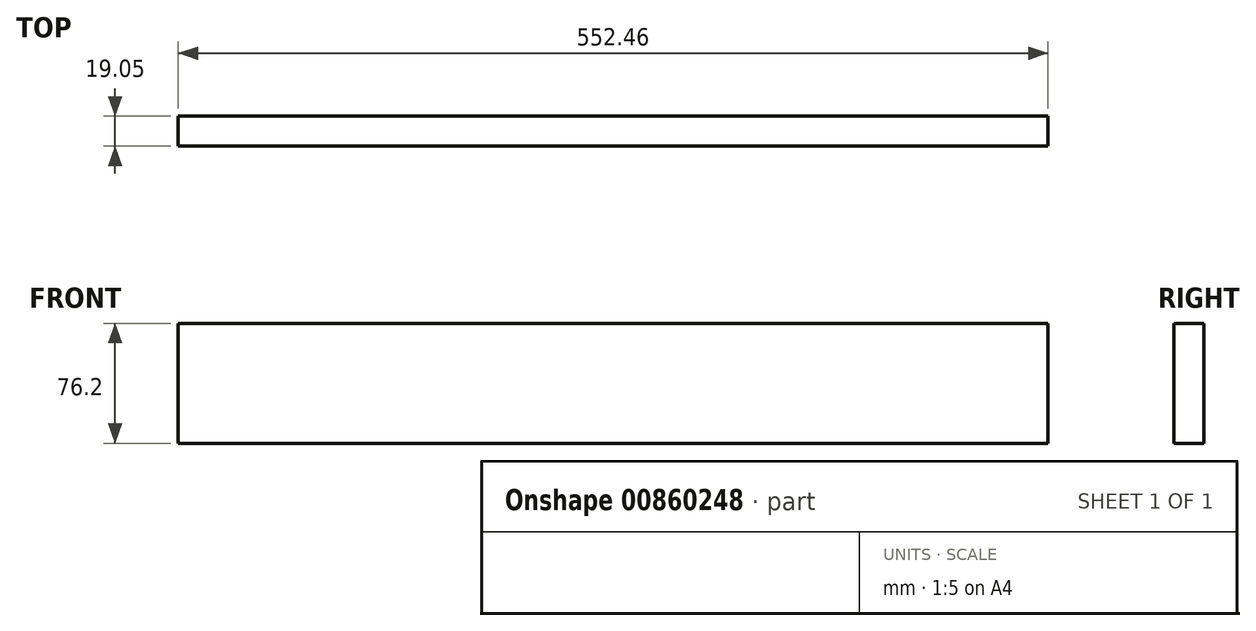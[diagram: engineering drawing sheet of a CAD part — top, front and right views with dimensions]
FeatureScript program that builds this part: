
annotation { "Feature Type Name" : "Feature", "Feature Type Description" : "" }
export const myFeature = defineFeature(function(context is Context, id is Id, definition is map)
    precondition{}
    {
        {
            var Q0;
            Q0=qCreatedBy(makeId("Front.planeOp"),FACE);
            var sketch = newSketch(context, id + "F0", { "sketchPlane" : qUnion([Q0])});
            skLineSegment(sketch, "E0.bottom", {"start": v(276.23, -38.1) * mm, "end": v(-276.23, -38.1) * mm});
            skLineSegment(sketch, "E0.top", {"start": v(276.23, 38.1) * mm, "end": v(-276.23, 38.1) * mm});
            skLineSegment(sketch, "E0.left", {"start": v(276.23, -38.1) * mm, "end": v(276.23, 38.1) * mm});
            skLineSegment(sketch, "E0.right", {"start": v(-276.23, -38.1) * mm, "end": v(-276.23, 38.1) * mm});
            skPoint(sketch, "E0.middle", {"position": v(0, 0) * mm});
            skSolve(sketch);
        }
        {
            var Q0;
            Q0 = qSketchRegion(id + "F0", true);
            extrude(context, id + "F1", {"entities" : qUnion([Q0]), "depth" : 19.05 * mm, "offsetDistance" : 25.4 * mm});
        }
    });
